# Revit family: M5OE-42HFN8-Q
name_source: partatom
category: Attrezzatura meccanica
units: mm (PartAtom-declared; Revit-internal decimal feet)

## family parameters
Basato su piano di lavoro = No
Condiviso = No
Mantieni orientamento annotazione = No
Numero OmniClass = 23.75.00.00
Punto di calcolo locali = No
Quota connettore circolare = Usa raggio
Sempre verticale = Sì
Taglio con vuoti quando caricato = No
Tipo di parte = Normale
Titolo OmniClass = Climate Control (HVAC)

## types (1)
- P10
    Air Flow = 3850.00 m³/h
    Casing color = SB2098
    Compressor = 1
    Depth = 410 mm  [stored 1.34514 ft]
    Gas = R32
    Gas pipe = 9.52 mm
    Gas pipe Radius = 4.76 mm
    Height = 810 mm
    Installation = Outdoor installation
    Liquid pipe = 6.35 mm  [stored 0.0208333 ft]
    Liquid pipe Radius = 3.175 mm  [stored 0.0104167 ft]
    Maximum Fuse Amps = 30 A
    Min cable selection (power wiring) = 3x4.0 mm2
    Minimum Circuit Amps = 22 A
    Modello = M5OE-42HFN8-Q
    Net Weight = 74.10 kg
    Power supply = 220-240V,1Ph, 50/60Hz
    Prospetto di default = 0 mm  [stored 0 ft]
    Width = 946 mm  [stored 3.10367 ft]
    clearance access behind = 300 mm
    clearance access front = 2000 mm  [stored 6.56168 ft]
    clearance access left = 300 mm
    clearance access right = 600 mm  [stored 1.9685 ft]

note: [stored X ft] marks values corroborated as IEEE doubles in the binary element streams (Revit-internal decimal feet)

## geometry (parser evidence)
native form markers: Blend x3, Sweep x17
no freeform markers — native parametric forms only
